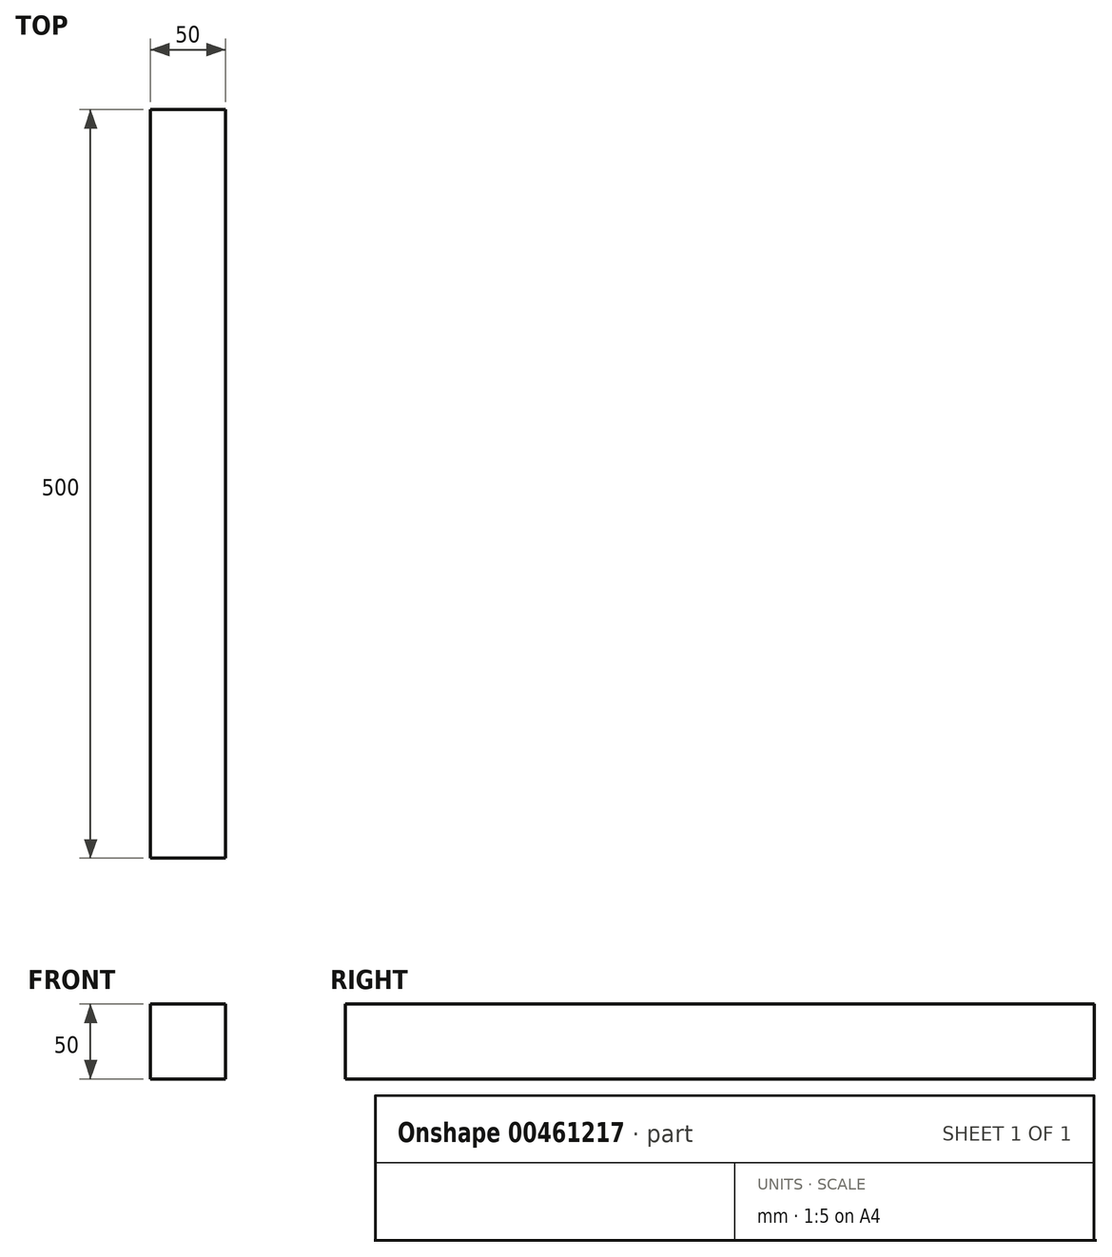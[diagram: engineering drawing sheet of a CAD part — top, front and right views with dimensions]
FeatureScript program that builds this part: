
annotation { "Feature Type Name" : "Feature", "Feature Type Description" : "" }
export const myFeature = defineFeature(function(context is Context, id is Id, definition is map)
    precondition{}
    {
        {
            var Q0;
            Q0=qCreatedBy(makeId("Front.planeOp"),FACE);
            var sketch = newSketch(context, id + "F0", { "sketchPlane" : qUnion([Q0])});
            skLineSegment(sketch, "E0.bottom", {"start": v(0, 0) * mm, "end": v(50, 0) * mm});
            skLineSegment(sketch, "E0.top", {"start": v(0, -50) * mm, "end": v(50, -50) * mm});
            skLineSegment(sketch, "E0.left", {"start": v(0, 0) * mm, "end": v(0, -50) * mm});
            skLineSegment(sketch, "E0.right", {"start": v(50, 0) * mm, "end": v(50, -50) * mm});
            skSolve(sketch);
        }
        {
            var Q0;
            Q0 = qSketchRegion(id + "F0", true);
            extrude(context, id + "F1", {"entities" : qUnion([Q0]), "depth" : 500 * mm});
        }
    });
